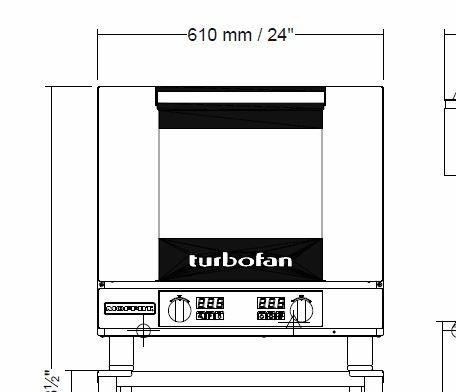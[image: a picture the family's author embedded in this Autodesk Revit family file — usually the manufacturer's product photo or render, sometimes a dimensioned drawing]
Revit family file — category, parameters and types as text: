
# Revit family: QF_MOFFAT_E23D3_NZ
name_source: partatom
category: Specialty Equipment
revit_build: Autodesk Revit 2014 (Build: 20130308_1515(x64)
units: mm (PartAtom-declared; Revit-internal decimal feet)

## types (1)
- QF_MOFFAT_E23D3_NZ
    Apparent Power = 2760 VA
    Cold Water Connection Height = 0 mm  [stored 0 ft]
    Cold Water Flow = 0 GPM
    Cold Water Maximum Pressure = 80.00 psi
    Cold Water Minimum Pressure = 20.00 psi
    Cold Water RI Height = 0 mm  [stored 0 ft]
    Cold Water Size = 1"
    Cold Water Temperature Recommended = 0 °F
    Conn Conduit = Yes
    Cycle = 50 Hz
    Depth = 643 mm  [stored 2.10958 ft]
    Description = HALF SIZE DIGITAL / ELECTRIC CONVECTION OVEN ON A STAINLESS STEEL STAND
    Elec Conn Connection Height = 0 mm  [stored 0 ft]
    Elec Conn RI Height = 0 mm  [stored 0 ft]
    Electrical Remarks = 230-240V, 50Hz, 1P+N+E, 3kW, 12A
    Exhaust RI Height = 0 mm  [stored 0 ft]
    Exhaust Static Press = 0.00 in-wg
    Exhaust Vent Depth = 0 mm  [stored 0 ft]
    Exhaust Vent Diameter = 0 mm  [stored 0 ft]
    Exhaust Vent Width = 0 mm  [stored 0 ft]
    Exhaust Volume = 0 CFM
    FL Amps = 12 A
    Foodservice Equipment Identifier = Yes
    Height = 1487 mm  [stored 4.87861 ft]
    Height of Stand = 880 mm  [stored 2.88714 ft]
    Identify Quantity as Lot = Yes
    Length = 610 mm  [stored 2.00131 ft]
    Manufacturer = MOFFAT
    Max Overcurrent Protection = 0 A
    Min Ckt Ampacity = 0 A
    Model = E23D3
    Number of Poles = 1
    Phase = 1
    URL = www.moffat.com.au
    URL Cutsheet = www.moffat.com.au
    Volts = 230 V
    Watts = 3000 W
    Weight in Pounds = 0

note: [stored X ft] marks values corroborated as IEEE doubles in the binary element streams (Revit-internal decimal feet)

## geometry (parser evidence)
native form markers: Blend x14, Sweep x7
no freeform markers — native parametric forms only
